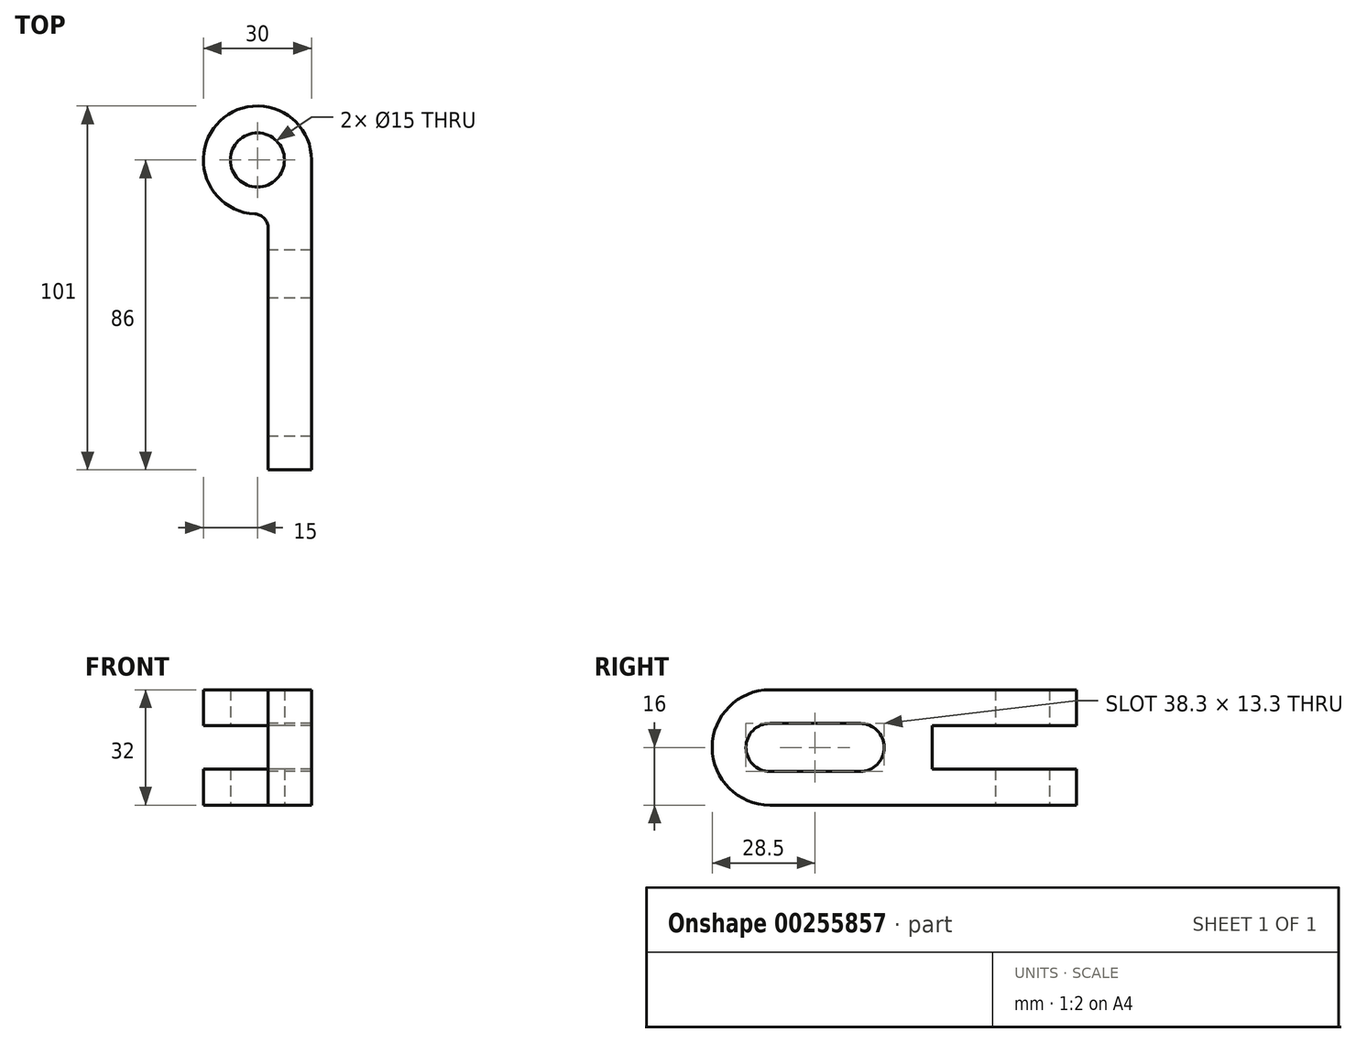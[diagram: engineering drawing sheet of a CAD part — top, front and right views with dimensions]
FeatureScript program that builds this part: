
annotation { "Feature Type Name" : "Feature", "Feature Type Description" : "" }
export const myFeature = defineFeature(function(context is Context, id is Id, definition is map)
    precondition{}
    {
        {
            var Q0;
            Q0=qCreatedBy(makeId("Top.planeOp"),FACE);
            var sketch = newSketch(context, id + "F0", { "sketchPlane" : qUnion([Q0])});
            skCircle(sketch, "E0", {"center": v(0, 0) * mm, "radius": 7.5 * mm});
            skArc(sketch, "E1", {"start": v(15, 0) * mm, "mid": v(-10.6, 10.6) * mm, "end": v(0, -15) * mm});
            skLineSegment(sketch, "E2.top", {"start": v(3, -86.09) * mm, "end": v(15, -86.09) * mm});
            skPoint(sketch, "E3.orphan", {"position": v(0, -0.09) * mm});
            skArc(sketch, "E4", {"start": v(0, -15) * mm, "mid": v(1.5, -14.92) * mm, "end": v(3, -14.7) * mm});
            skLineSegment(sketch, "E5", {"start": v(15, -86.09) * mm, "end": v(15, 0) * mm});
            skLineSegment(sketch, "E6", {"start": v(3, -86.09) * mm, "end": v(3, -14.7) * mm});
            skSolve(sketch);
        }
        {
            var Q0;
            Q0 = qSketchRegion(id + "F0", true);
            extrude(context, id + "F1", {"entities" : qUnion([Q0]), "endBound" : BoundingType.SYMMETRIC, "depth" : 32 * mm});
        }
        {
            var Q0;
            Q0=qCreatedBy(makeId("Right.planeOp"),FACE);
            cPlane(context, id + "F2", {"entities" : qUnion([Q0]), "cplaneType" : CPlaneType.OFFSET, "offset" : 25 * mm, "oppositeDirection" : true, "width" : 150 * mm, "height" : 150 * mm});
        }
        {
            var Q0;
            Q0=makeQuery(id+"F1.opExtrude","SWEPT_FACE",FACE,{"disambiguationData":[OSD([sQuery(id+"F0.wireOp",EDGE,"E6")])]});
            var sketch = newSketch(context, id + "F3", { "sketchPlane" : qUnion([Q0])});
            skLineSegment(sketch, "E7.0.0", {"start": v(-15, -16) * mm, "end": v(15, -16) * mm});
            skLineSegment(sketch, "E7.0.1", {"start": v(14.7, -16) * mm, "end": v(14.7, 16) * mm});
            skLineSegment(sketch, "E7.0.2", {"start": v(15, 16) * mm, "end": v(-15, 16) * mm});
            skLineSegment(sketch, "E7.0.3", {"start": v(0, 16) * mm, "end": v(0, -16) * mm});
            skLineSegment(sketch, "E8.bottom", {"start": v(45, -6.65) * mm, "end": v(70, -6.65) * mm});
            skLineSegment(sketch, "E8.top", {"start": v(45, 6.65) * mm, "end": v(70, 6.65) * mm});
            skPoint(sketch, "E8.middle", {"position": v(57.5, 0) * mm});
            skLineSegment(sketch, "E9.bottom", {"start": v(-25, 6) * mm, "end": v(25, 6) * mm});
            skLineSegment(sketch, "E9.top", {"start": v(-25, -6) * mm, "end": v(25, -6) * mm});
            skLineSegment(sketch, "E9.left", {"start": v(-25, 6) * mm, "end": v(-25, -6) * mm});
            skLineSegment(sketch, "E9.right", {"start": v(25, 6) * mm, "end": v(25, -6) * mm});
            skPoint(sketch, "E9.middle", {"position": v(0, 0) * mm});
            skArc(sketch, "E10", {"start": v(45, -6.65) * mm, "mid": v(38.35, 0) * mm, "end": v(45, 6.65) * mm});
            skArc(sketch, "E11", {"start": v(70, -6.65) * mm, "mid": v(76.65, 0) * mm, "end": v(70, 6.65) * mm});
            skArc(sketch, "E12", {"start": v(70, -16) * mm, "mid": v(86, 0) * mm, "end": v(70, 16) * mm});
            skSolve(sketch);
        }
        {
            var Q0;
            {var subQ0=sQuery(id+"F3.wireOp",EDGE,"E12");Q0=makeQuery(id+"F3.imprint","IMPRINT",FACE,{"disambiguationData":[TD([[makeQuery(id+"F3.imprint","IMPRINT",EDGE,{"derivedFrom":subQ0}),-1.0]])]});}
            var Q1;
            Q1=makeQuery(id+"F3.imprint","IMPRINT",FACE,{"disambiguationData":[TD([[makeQuery(id+"F3.imprint","IMPRINT",EDGE,{"derivedFrom":sQuery(id+"F3.wireOp",EDGE,"E8.bottom")}),1.0]])]});
            var Q2;
            {var subQ5=sQuery(id+"F3.wireOp",EDGE,"E9.right");Q2=makeQuery(id+"F3.imprint","IMPRINT",FACE,{"disambiguationData":[TD([[makeQuery(id+"F3.imprint","IMPRINT",EDGE,{"derivedFrom":subQ5}),-1.0]])]});}
            extrude(context, id + "F4", {"entities" : qUnion([Q0, Q1, Q2]), "operationType" : NewBodyOperationType.REMOVE, "endBound" : BoundingType.THROUGH_ALL, "oppositeDirection" : true, "depth" : 25 * mm});
        }
        {
            var Q0;
            Q0=qCreatedBy(id+"F2.planeOp",FACE);
            var sketch = newSketch(context, id + "F5", { "sketchPlane" : qUnion([Q0])});
            skLineSegment(sketch, "E13.bottom", {"start": v(-18.57, 6) * mm, "end": v(18.57, 6) * mm});
            skLineSegment(sketch, "E13.top", {"start": v(-18.57, -6) * mm, "end": v(18.57, -6) * mm});
            skLineSegment(sketch, "E13.left", {"start": v(-18.57, 6) * mm, "end": v(-18.57, -6) * mm});
            skLineSegment(sketch, "E13.right", {"start": v(18.57, 6) * mm, "end": v(18.57, -6) * mm});
            skPoint(sketch, "E13.middle", {"position": v(0, 0) * mm});
            skSolve(sketch);
        }
        {
            var Q0;
            Q0=makeQuery(id+"F5.imprint","IMPRINT",FACE,{"disambiguationData":[TD([[makeQuery(id+"F5.imprint","IMPRINT",EDGE,{"derivedFrom":sQuery(id+"F5.wireOp",EDGE,"E13.bottom")}),-1.0]])]});
            extrude(context, id + "F6", {"entities" : qUnion([Q0]), "operationType" : NewBodyOperationType.REMOVE, "endBound" : BoundingType.THROUGH_ALL, "depth" : 25 * mm});
        }
        {
            var Q0;
            {var subQ0=sQuery(id+"F0.wireOp",EDGE,"E6");var subQ1=sQuery(id+"F0.wireOp",EDGE,"E4");Q0=makeQuery(id+"F4.boolean.opBoolean","SPLIT",EDGE,{"disambiguationData":[TD([makeQuery(id+"F4.opExtrude","SWEPT_FACE",FACE,{"disambiguationData":[OSD([sQuery(id+"F3.wireOp",EDGE,"E9.top")])]})])],"derivedFrom":makeQuery(id+"F1.opExtrude","SWEPT_EDGE",EDGE,{"disambiguationData":[OSD([subQ1,subQ0])]})});}
            var Q1;
            {var subQ0=sQuery(id+"F0.wireOp",EDGE,"E6");var subQ1=sQuery(id+"F0.wireOp",EDGE,"E4");Q1=makeQuery(id+"F4.boolean.opBoolean","SPLIT",EDGE,{"disambiguationData":[TD([makeQuery(id+"F4.opExtrude","SWEPT_FACE",FACE,{"disambiguationData":[OSD([sQuery(id+"F3.wireOp",EDGE,"E9.bottom")])]})])],"derivedFrom":makeQuery(id+"F1.opExtrude","SWEPT_EDGE",EDGE,{"disambiguationData":[OSD([subQ1,subQ0])]})});}
            fillet(context, id + "F7", {"entities" : qUnion([Q0, Q1]), "radius" : 4 * mm, "tangentPropagation" : true, "allowEdgeOverflow" : false});
        }
    });
